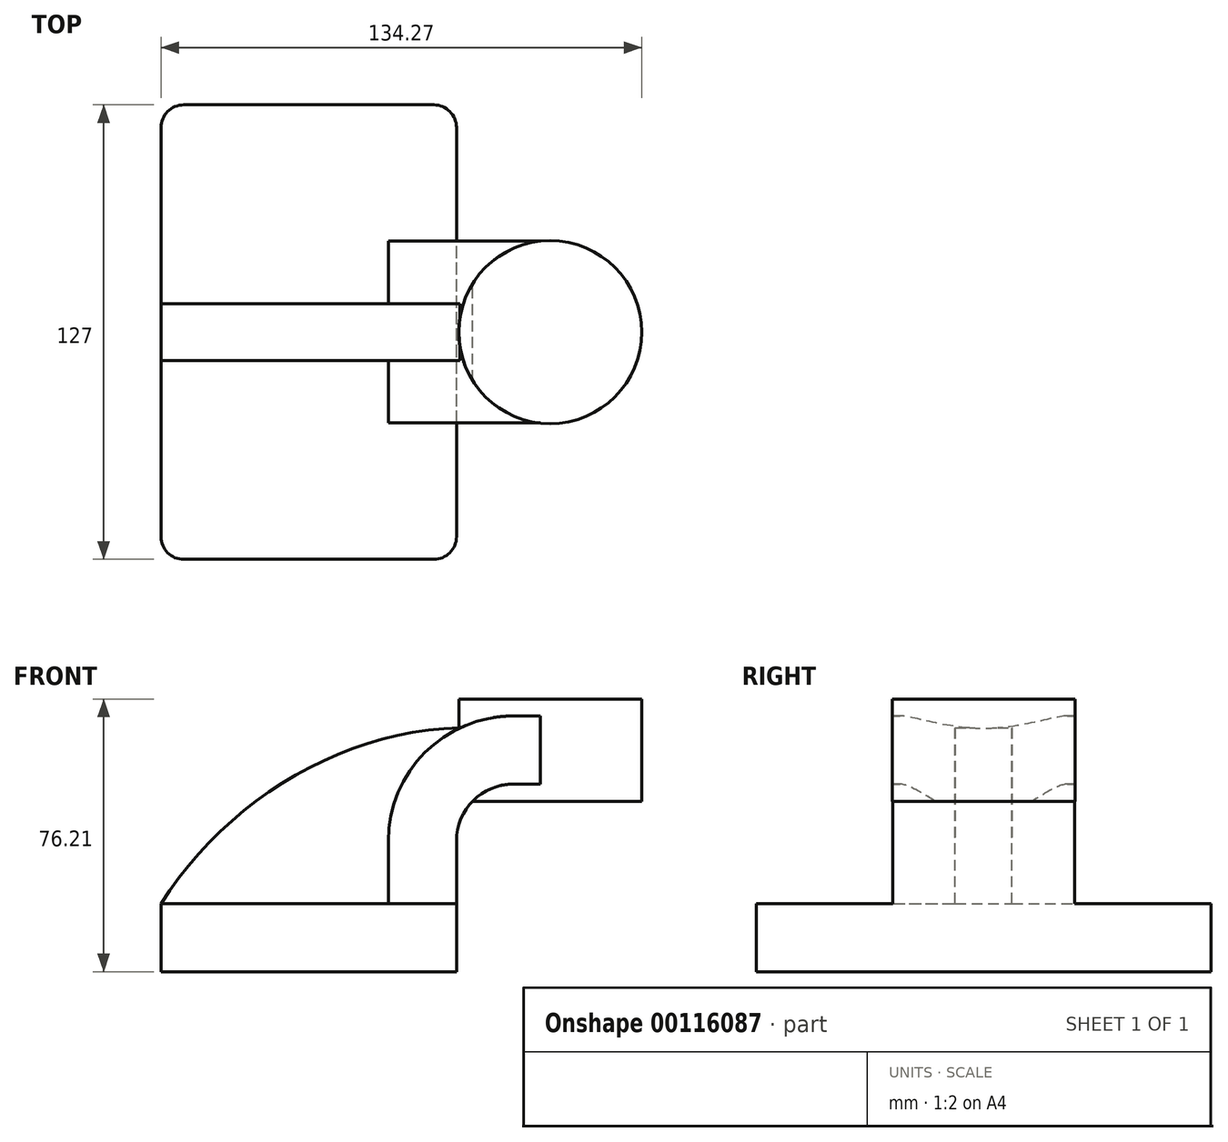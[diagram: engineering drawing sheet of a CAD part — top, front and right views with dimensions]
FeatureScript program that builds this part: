
annotation { "Feature Type Name" : "Feature", "Feature Type Description" : "" }
export const myFeature = defineFeature(function(context is Context, id is Id, definition is map)
    precondition{}
    {
        {
            var Q0;
            Q0=qCreatedBy(makeId("Front.planeOp"),FACE);
            var sketch = newSketch(context, id + "F0", { "sketchPlane" : qUnion([Q0])});
            skLineSegment(sketch, "E0.bottom", {"start": v(41.28, -9.52) * mm, "end": v(-41.27, -9.53) * mm});
            skLineSegment(sketch, "E0.top", {"start": v(41.27, 9.53) * mm, "end": v(-41.28, 9.53) * mm});
            skLineSegment(sketch, "E0.left", {"start": v(41.28, -9.52) * mm, "end": v(41.28, 9.53) * mm});
            skLineSegment(sketch, "E0.right", {"start": v(-41.27, -9.53) * mm, "end": v(-41.28, 9.53) * mm});
            skPoint(sketch, "E0.middle", {"position": v(0, 0) * mm});
            skLineSegment(sketch, "E1.bottom", {"start": v(93, 38.1) * mm, "end": v(42.2, 38.1) * mm});
            skLineSegment(sketch, "E1.top", {"start": v(93, 66.68) * mm, "end": v(42.2, 66.68) * mm});
            skLineSegment(sketch, "E1.left", {"start": v(93, 38.1) * mm, "end": v(93, 66.68) * mm});
            skLineSegment(sketch, "E1.right", {"start": v(42.2, 38.1) * mm, "end": v(42.2, 66.68) * mm});
            skPoint(sketch, "E1.middle", {"position": v(67.6, 52.39) * mm});
            skLineSegment(sketch, "E2", {"start": v(41.27, 9.53) * mm, "end": v(41.27, 27) * mm});
            skArc(sketch, "E3", {"start": v(41.27, 27) * mm, "mid": v(45.92, 38.23) * mm, "end": v(57.15, 42.88) * mm});
            skLineSegment(sketch, "E4", {"start": v(57.15, 42.88) * mm, "end": v(67.44, 42.88) * mm});
            skLineSegment(sketch, "E5.0", {"start": v(57.15, 61.93) * mm, "end": v(67.44, 61.93) * mm});
            skArc(sketch, "E5.1", {"start": v(22.23, 27) * mm, "mid": v(32.45, 51.7) * mm, "end": v(57.15, 61.93) * mm});
            skLineSegment(sketch, "E5.2", {"start": v(22.22, 9.53) * mm, "end": v(22.22, 27) * mm});
            skLineSegment(sketch, "E6", {"start": v(67.44, 66.68) * mm, "end": v(67.44, 38.1) * mm});
            skFitSpline(sketch, "E7", {"points": [v(-41.28, 9.53) * mm, v(42.2, 58.56) * mm], "startDerivative": vector(53.83, 84.12) * mm, "endDerivative": vector(102.15, 2.36) * mm});
            skSolve(sketch);
        }
        {
            var Q0;
            Q0=makeQuery(id+"F0.imprint","IMPRINT",FACE,{"disambiguationData":[TD([[makeQuery(id+"F0.imprint","IMPRINT",EDGE,{"derivedFrom":sQuery(id+"F0.wireOp",EDGE,"E0.bottom")}),-1.0]])]});
            extrude(context, id + "F1", {"entities" : qUnion([Q0]), "endBound" : BoundingType.SYMMETRIC, "depth" : 127 * mm});
        }
        {
            var Q0;
            {var subQ0=sQuery(id+"F0.wireOp",EDGE,"E2");Q0=makeQuery(id+"F0.imprint","IMPRINT",FACE,{"disambiguationData":[TD([[makeQuery(id+"F0.imprint","IMPRINT",EDGE,{"derivedFrom":subQ0}),1.0]])]});}
            var Q1;
            {var subQ0=sQuery(id+"F0.wireOp",EDGE,"E4");Q1=makeQuery(id+"F0.imprint","IMPRINT",FACE,{"disambiguationData":[TD([[makeQuery(id+"F0.imprint","IMPRINT",EDGE,{"derivedFrom":subQ0}),1.0]])]});}
            extrude(context, id + "F2", {"entities" : qUnion([Q0, Q1]), "operationType" : NewBodyOperationType.ADD, "endBound" : BoundingType.SYMMETRIC, "depth" : 50.8 * mm});
        }
        {
            var Q0;
            {var subQ2=sQuery(id+"F0.wireOp",EDGE,"E5.2");Q0=makeQuery(id+"F0.imprint","IMPRINT",FACE,{"disambiguationData":[TD([[makeQuery(id+"F0.imprint","IMPRINT",EDGE,{"derivedFrom":subQ2}),1.0]])]});}
            extrude(context, id + "F3", {"entities" : qUnion([Q0]), "operationType" : NewBodyOperationType.ADD, "endBound" : BoundingType.SYMMETRIC, "depth" : 15.88 * mm});
        }
        {
            var Q0;
            {var subQ0=sQuery(id+"F0.wireOp",EDGE,"E1.left");Q0=makeQuery(id+"F0.imprint","IMPRINT",FACE,{"disambiguationData":[TD([[makeQuery(id+"F0.imprint","IMPRINT",EDGE,{"derivedFrom":subQ0}),1.0]])]});}
            var Q1;
            Q1=sQuery(id+"F0.wireOp",EDGE,"E6");
            revolve(context, id + "F4", {"operationType" : NewBodyOperationType.ADD, "entities" : qUnion([Q0]), "axis" : qUnion([Q1]), "revolveType" : RevolveType.FULL});
        }
        {
            var Q0;
            Q0=makeQuery(id+"F1.opExtrude","CAP_EDGE",EDGE,{"disambiguationData":[OSD([sQuery(id+"F0.wireOp",EDGE,"E0.left")])],"isStart":false});
            var Q1;
            Q1=makeQuery(id+"F1.opExtrude","CAP_EDGE",EDGE,{"disambiguationData":[OSD([sQuery(id+"F0.wireOp",EDGE,"E0.right")])],"isStart":false});
            var Q2;
            Q2=makeQuery(id+"F1.opExtrude","CAP_EDGE",EDGE,{"disambiguationData":[OSD([sQuery(id+"F0.wireOp",EDGE,"E0.left")])],"isStart":true});
            var Q3;
            Q3=makeQuery(id+"F1.opExtrude","CAP_EDGE",EDGE,{"disambiguationData":[OSD([sQuery(id+"F0.wireOp",EDGE,"E0.right")])],"isStart":true});
            fillet(context, id + "F5", {"entities" : qUnion([Q0, Q1, Q2, Q3]), "radius" : 6.35 * mm, "tangentPropagation" : true, "allowEdgeOverflow" : false});
        }
    });
